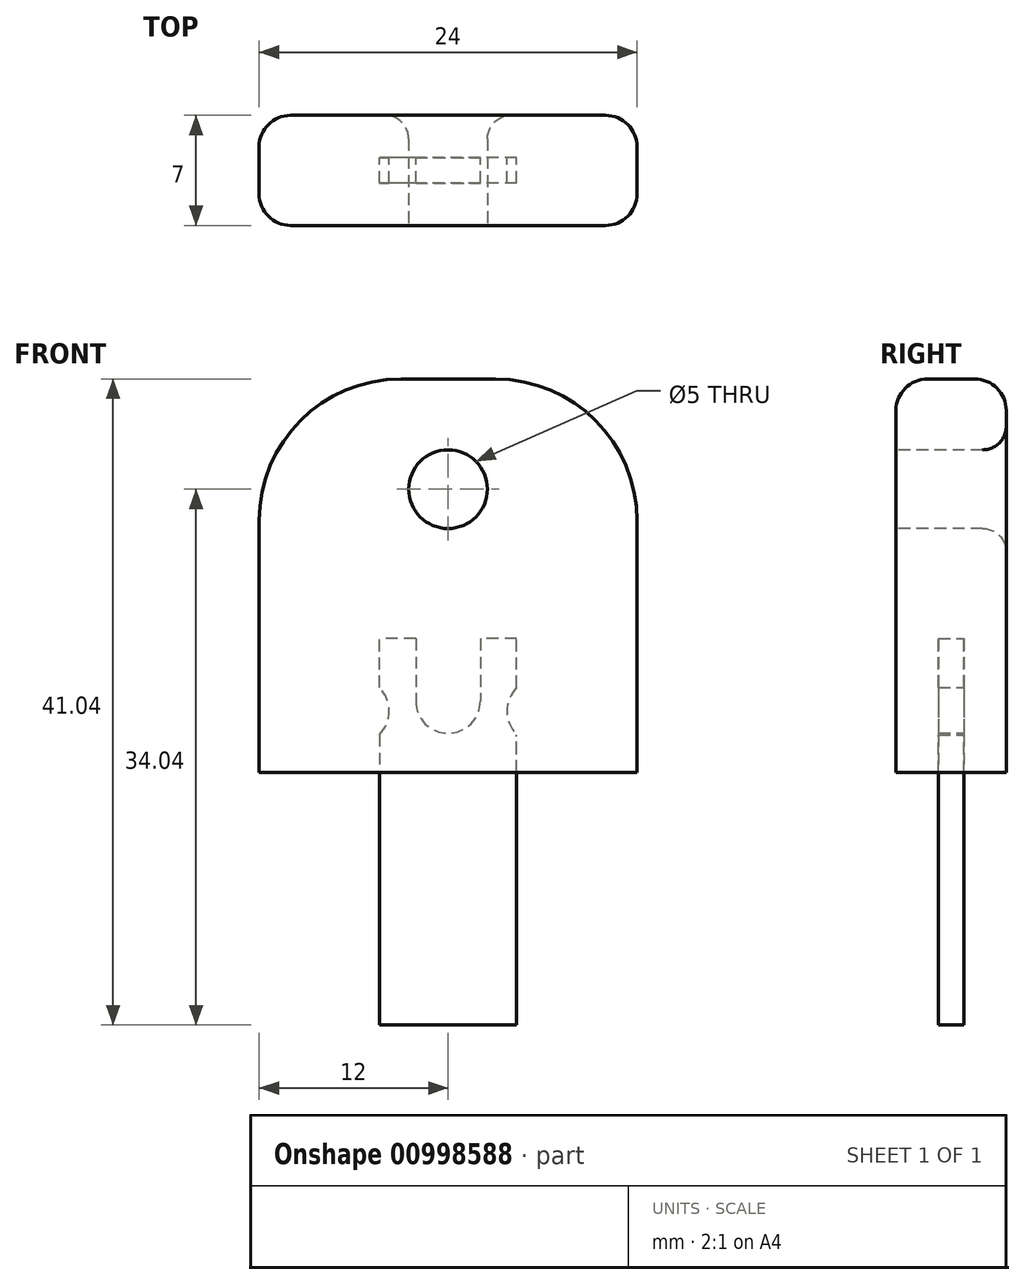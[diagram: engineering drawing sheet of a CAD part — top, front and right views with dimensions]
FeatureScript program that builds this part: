
annotation { "Feature Type Name" : "Feature", "Feature Type Description" : "" }
export const myFeature = defineFeature(function(context is Context, id is Id, definition is map)
    precondition{}
    {
        {
            var Q0;
            Q0=qCreatedBy(makeId("Front.planeOp"),FACE);
            var sketch = newSketch(context, id + "F0", { "sketchPlane" : qUnion([Q0])});
            skLineSegment(sketch, "E0.bottom", {"start": v(-12, 25) * mm, "end": v(12, 25) * mm});
            skLineSegment(sketch, "E0.top", {"start": v(-12, 0) * mm, "end": v(12, 0) * mm});
            skLineSegment(sketch, "E0.left", {"start": v(-12, 25) * mm, "end": v(-12, 0) * mm});
            skLineSegment(sketch, "E0.right", {"start": v(12, 25) * mm, "end": v(12, 0) * mm});
            skSolve(sketch);
        }
        {
            var Q0;
            Q0 = qSketchRegion(id + "F0", true);
            extrude(context, id + "F1", {"entities" : qUnion([Q0]), "endBound" : BoundingType.SYMMETRIC, "depth" : 7 * mm, "offsetDistance" : 25 * mm});
        }
        {
            var Q0;
            Q0=makeQuery(id+"F1.opExtrude","CAP_EDGE",EDGE,{"disambiguationData":[OSD([sQuery(id+"F0.wireOp",EDGE,"E0.bottom")])],"isStart":false});
            var Q1;
            Q1=makeQuery(id+"F1.opExtrude","CAP_EDGE",EDGE,{"disambiguationData":[OSD([sQuery(id+"F0.wireOp",EDGE,"E0.bottom")])],"isStart":true});
            var Q2;
            Q2=makeQuery(id+"F1.opExtrude","CAP_EDGE",EDGE,{"disambiguationData":[OSD([sQuery(id+"F0.wireOp",EDGE,"E0.left")])],"isStart":false});
            var Q3;
            Q3=makeQuery(id+"F1.opExtrude","CAP_EDGE",EDGE,{"disambiguationData":[OSD([sQuery(id+"F0.wireOp",EDGE,"E0.left")])],"isStart":true});
            var Q4;
            Q4=makeQuery(id+"F1.opExtrude","CAP_EDGE",EDGE,{"disambiguationData":[OSD([sQuery(id+"F0.wireOp",EDGE,"E0.right")])],"isStart":false});
            var Q5;
            Q5=makeQuery(id+"F1.opExtrude","CAP_EDGE",EDGE,{"disambiguationData":[OSD([sQuery(id+"F0.wireOp",EDGE,"E0.right")])],"isStart":true});
            fillet(context, id + "F2", {"entities" : qUnion([Q0, Q1, Q2, Q3, Q4, Q5]), "radius" : 2 * mm, "tangentPropagation" : true, "allowEdgeOverflow" : false});
        }
        {
            var Q0;
            Q0=qCreatedBy(makeId("Front.planeOp"),FACE);
            var sketch = newSketch(context, id + "F3", { "sketchPlane" : qUnion([Q0])});
            skLineSegment(sketch, "E1", {"start": v(-4.35, 8.5) * mm, "end": v(-4.35, -16.04) * mm, "construction": true});
            skLineSegment(sketch, "E2", {"start": v(4.35, 8.5) * mm, "end": v(4.35, -16.04) * mm, "construction": true});
            skLineSegment(sketch, "E3", {"start": v(-4.35, 3.9) * mm, "end": v(4.35, 3.9) * mm, "construction": true});
            skLineSegment(sketch, "E4", {"start": v(-4.35, 5.4) * mm, "end": v(-4.35, 8.5) * mm});
            skLineSegment(sketch, "E5", {"start": v(4.35, 8.5) * mm, "end": v(2.05, 8.5) * mm});
            skLineSegment(sketch, "E6", {"start": v(4.35, 5.4) * mm, "end": v(4.35, 8.5) * mm});
            skLineSegment(sketch, "E7", {"start": v(-4.35, 2.4) * mm, "end": v(-4.35, -16.04) * mm});
            skLineSegment(sketch, "E8", {"start": v(4.35, -16.04) * mm, "end": v(-4.35, -16.04) * mm});
            skLineSegment(sketch, "E9", {"start": v(4.35, -16.04) * mm, "end": v(4.35, 2.4) * mm});
            skArc(sketch, "E10", {"start": v(-4.35, 5.4) * mm, "mid": v(-3.75, 3.9) * mm, "end": v(-4.35, 2.4) * mm});
            skArc(sketch, "E11", {"start": v(4.35, 5.4) * mm, "mid": v(3.75, 3.9) * mm, "end": v(4.35, 2.4) * mm});
            skLineSegment(sketch, "E12", {"start": v(-2.05, 8.5) * mm, "end": v(-2.05, 4.55) * mm});
            skLineSegment(sketch, "E13", {"start": v(2.05, 8.5) * mm, "end": v(2.05, 4.55) * mm});
            skArc(sketch, "E14", {"start": v(-2.05, 4.55) * mm, "mid": v(0, 2.5) * mm, "end": v(2.05, 4.55) * mm});
            skLineSegment(sketch, "E15.trimOffspring", {"start": v(-2.05, 8.5) * mm, "end": v(-4.35, 8.5) * mm});
            skSolve(sketch);
        }
        {
            var Q0;
            Q0 = qSketchRegion(id + "F3", true);
            extrude(context, id + "F4", {"entities" : qUnion([Q0]), "endBound" : BoundingType.SYMMETRIC, "depth" : 1.6 * mm, "offsetDistance" : 25 * mm});
        }
        {
            var Q0;
            Q0=makeQuery(id+"F1.opExtrude","CAP_FACE",FACE,{"disambiguationData":[OSD([sQuery(id+"F0.wireOp",EDGE,"E0.bottom"),sQuery(id+"F0.wireOp",EDGE,"E0.top"),sQuery(id+"F0.wireOp",EDGE,"E0.left"),sQuery(id+"F0.wireOp",EDGE,"E0.right")])],"isStart":false});
            var sketch = newSketch(context, id + "F5", { "sketchPlane" : qUnion([Q0])});
            skCircle(sketch, "E16", {"center": v(0, 18) * mm, "radius": 2.5 * mm});
            skSolve(sketch);
        }
        {
            var Q0;
            Q0 = qSketchRegion(id + "F5", true);
            extrude(context, id + "F6", {"entities" : qUnion([Q0]), "operationType" : NewBodyOperationType.REMOVE, "endBound" : BoundingType.THROUGH_ALL, "oppositeDirection" : true, "depth" : 25 * mm, "offsetDistance" : 25 * mm});
        }
        {
            var Q0;
            Q0=makeQuery(id+"F4.opExtrude","SWEPT_BODY",BODY,{"disambiguationData":[OSD([sQuery(id+"F3.wireOp",EDGE,"1gXd74iX-XAiX-hnWL-2aIT-e30dxOGhU8RL"),sQuery(id+"F3.wireOp",EDGE,"gwzKI6ou-c3dz-wP7X-TlEm-UqFZSVXnKC0w"),sQuery(id+"F3.wireOp",EDGE,"E4"),sQuery(id+"F3.wireOp",EDGE,"E5"),sQuery(id+"F3.wireOp",EDGE,"E6"),sQuery(id+"F3.wireOp",EDGE,"E7"),sQuery(id+"F3.wireOp",EDGE,"E8"),sQuery(id+"F3.wireOp",EDGE,"E9")])]});
            var Q1;
            Q1=makeQuery(id+"F1.opExtrude","SWEPT_BODY",BODY,{"disambiguationData":[OSD([sQuery(id+"F0.wireOp",EDGE,"E0.bottom"),sQuery(id+"F0.wireOp",EDGE,"E0.top"),sQuery(id+"F0.wireOp",EDGE,"E0.left"),sQuery(id+"F0.wireOp",EDGE,"E0.right")])]});
            booleanBodies(context, id + "F7", {"operationType" : BooleanOperationType.SUBTRACTION, "tools" : qUnion([Q0]), "targets" : qUnion([Q1]), "keepTools" : true});
        }
        {
            var Q0;
            Q0=makeQuery(id+"F6.boolean.opBoolean","INTERSECT",EDGE,{"derivedFrom":[makeQuery(id+"F1.opExtrude","CAP_FACE",FACE,{"disambiguationData":[OSD([sQuery(id+"F0.wireOp",EDGE,"E0.bottom"),sQuery(id+"F0.wireOp",EDGE,"E0.top"),sQuery(id+"F0.wireOp",EDGE,"E0.left"),sQuery(id+"F0.wireOp",EDGE,"E0.right")])],"isStart":true}),makeQuery(id+"F6.opExtrude","SWEPT_FACE",FACE,{"disambiguationData":[OSD([sQuery(id+"F5.wireOp",EDGE,"E16")])]})]});
            var Q1;
            Q1=makeQuery(id+"F6.boolean.opBoolean","COPY",EDGE,{"derivedFrom":makeQuery(id+"F6.opExtrude","CAP_EDGE",EDGE,{"disambiguationData":[OSD([sQuery(id+"F5.wireOp",EDGE,"E16")])],"isStart":true})});
            fillet(context, id + "F8", {"entities" : qUnion([Q0, Q1]), "radius" : 1.5 * mm, "tangentPropagation" : true, "allowEdgeOverflow" : false});
        }
        {
            var Q0;
            Q0=makeQuery(id+"F1.opExtrude","SWEPT_EDGE",EDGE,{"disambiguationData":[OSD([sQuery(id+"F0.wireOp",EDGE,"E0.bottom"),sQuery(id+"F0.wireOp",EDGE,"E0.right")])]});
            var Q1;
            Q1=makeQuery(id+"F1.opExtrude","SWEPT_EDGE",EDGE,{"disambiguationData":[OSD([sQuery(id+"F0.wireOp",EDGE,"E0.bottom"),sQuery(id+"F0.wireOp",EDGE,"E0.left")])]});
            fillet(context, id + "F9", {"entities" : qUnion([Q0, Q1]), "radius" : 9 * mm, "tangentPropagation" : true, "allowEdgeOverflow" : false});
        }
    });
